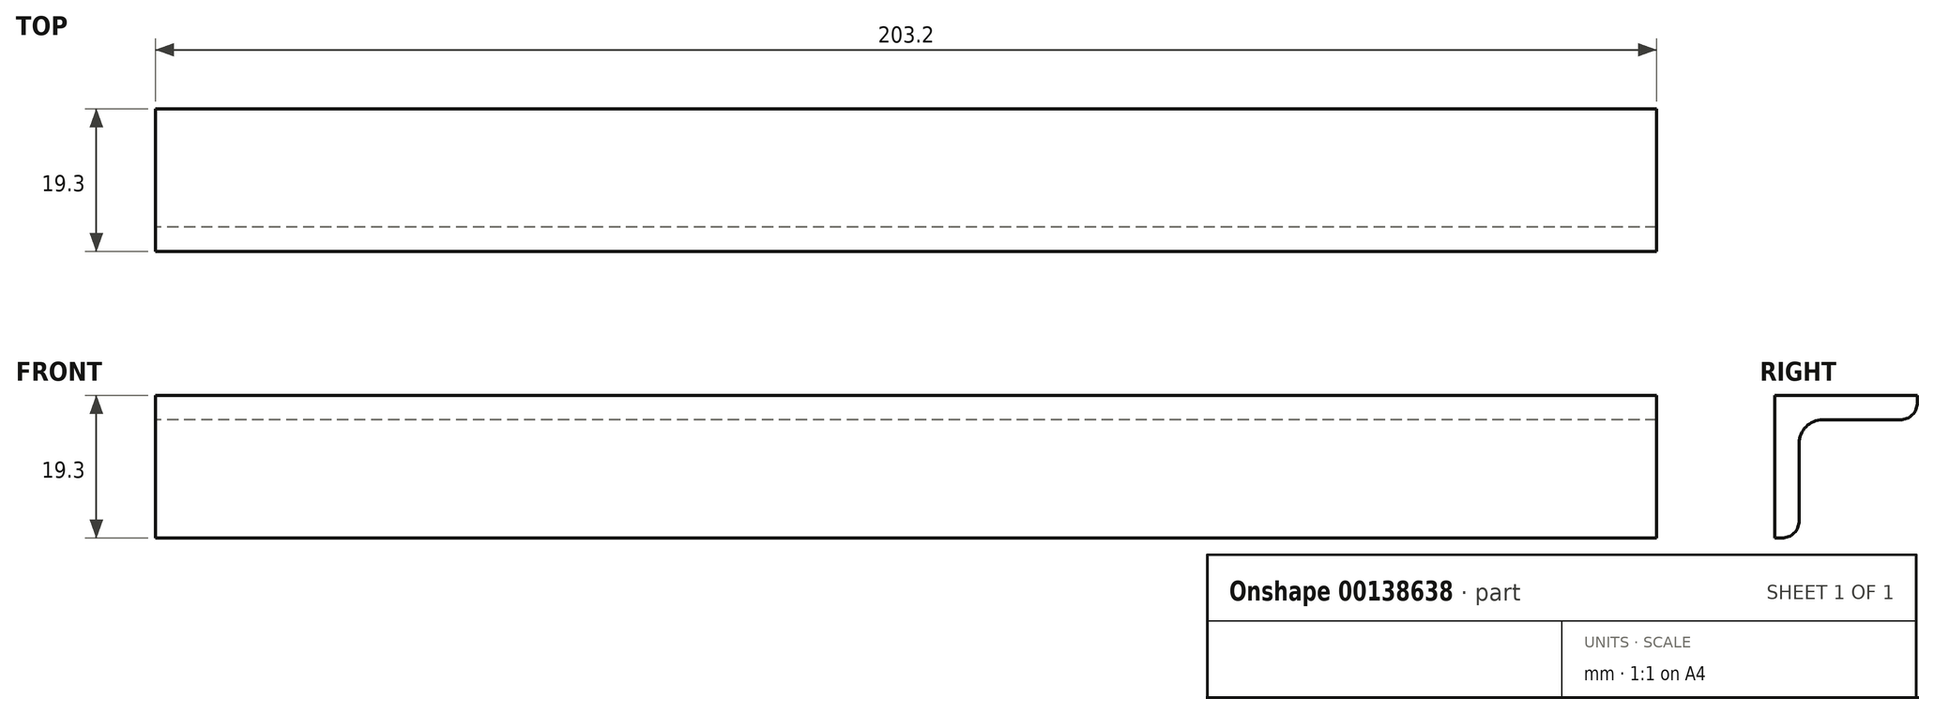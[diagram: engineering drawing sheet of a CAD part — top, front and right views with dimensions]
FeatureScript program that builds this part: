
annotation { "Feature Type Name" : "Feature", "Feature Type Description" : "" }
export const myFeature = defineFeature(function(context is Context, id is Id, definition is map)
    precondition{}
    {
        {
            var Q0;
            Q0=qCreatedBy(makeId("Right.planeOp"),FACE);
            var sketch = newSketch(context, id + "F0", { "sketchPlane" : qUnion([Q0])});
            skLineSegment(sketch, "E0.bottom", {"start": v(0, 0) * mm, "end": v(19.3, 0) * mm});
            skLineSegment(sketch, "E0.left", {"start": v(0, 0) * mm, "end": v(0, -19.3) * mm});
            skLineSegment(sketch, "E1.bottom", {"start": v(6.48, -3.3) * mm, "end": v(16.94, -3.3) * mm});
            skLineSegment(sketch, "E2", {"start": v(0.94, -19.3) * mm, "end": v(0, -19.3) * mm});
            skLineSegment(sketch, "E3", {"start": v(19.3, 0) * mm, "end": v(19.3, -0.94) * mm});
            skLineSegment(sketch, "E4", {"start": v(3.3, -16.94) * mm, "end": v(3.3, -6.48) * mm});
            skPoint(sketch, "E5.visualSharp", {"position": v(3.3, -3.3) * mm});
            skArc(sketch, "E5.filletArc", {"start": v(6.48, -3.3) * mm, "mid": v(4.23, -4.23) * mm, "end": v(3.3, -6.48) * mm});
            skPoint(sketch, "E6.visualSharp", {"position": v(3.3, -19.3) * mm});
            skArc(sketch, "E6.filletArc", {"start": v(0.94, -19.3) * mm, "mid": v(2.61, -18.61) * mm, "end": v(3.3, -16.94) * mm});
            skPoint(sketch, "E7.visualSharp", {"position": v(19.3, -3.3) * mm});
            skArc(sketch, "E7.filletArc", {"start": v(16.94, -3.3) * mm, "mid": v(18.61, -2.61) * mm, "end": v(19.3, -0.94) * mm});
            skSolve(sketch);
        }
        {
            var Q0;
            Q0=makeQuery(id+"F0.imprint","IMPRINT",FACE,{"disambiguationData":[TD([[makeQuery(id+"F0.imprint","IMPRINT",EDGE,{"derivedFrom":sQuery(id+"F0.wireOp",EDGE,"E0.bottom")}),-1.0]])]});
            extrude(context, id + "F1", {"entities" : qUnion([Q0]), "endBound" : BoundingType.SYMMETRIC, "depth" : 203.2 * mm});
        }
    });
